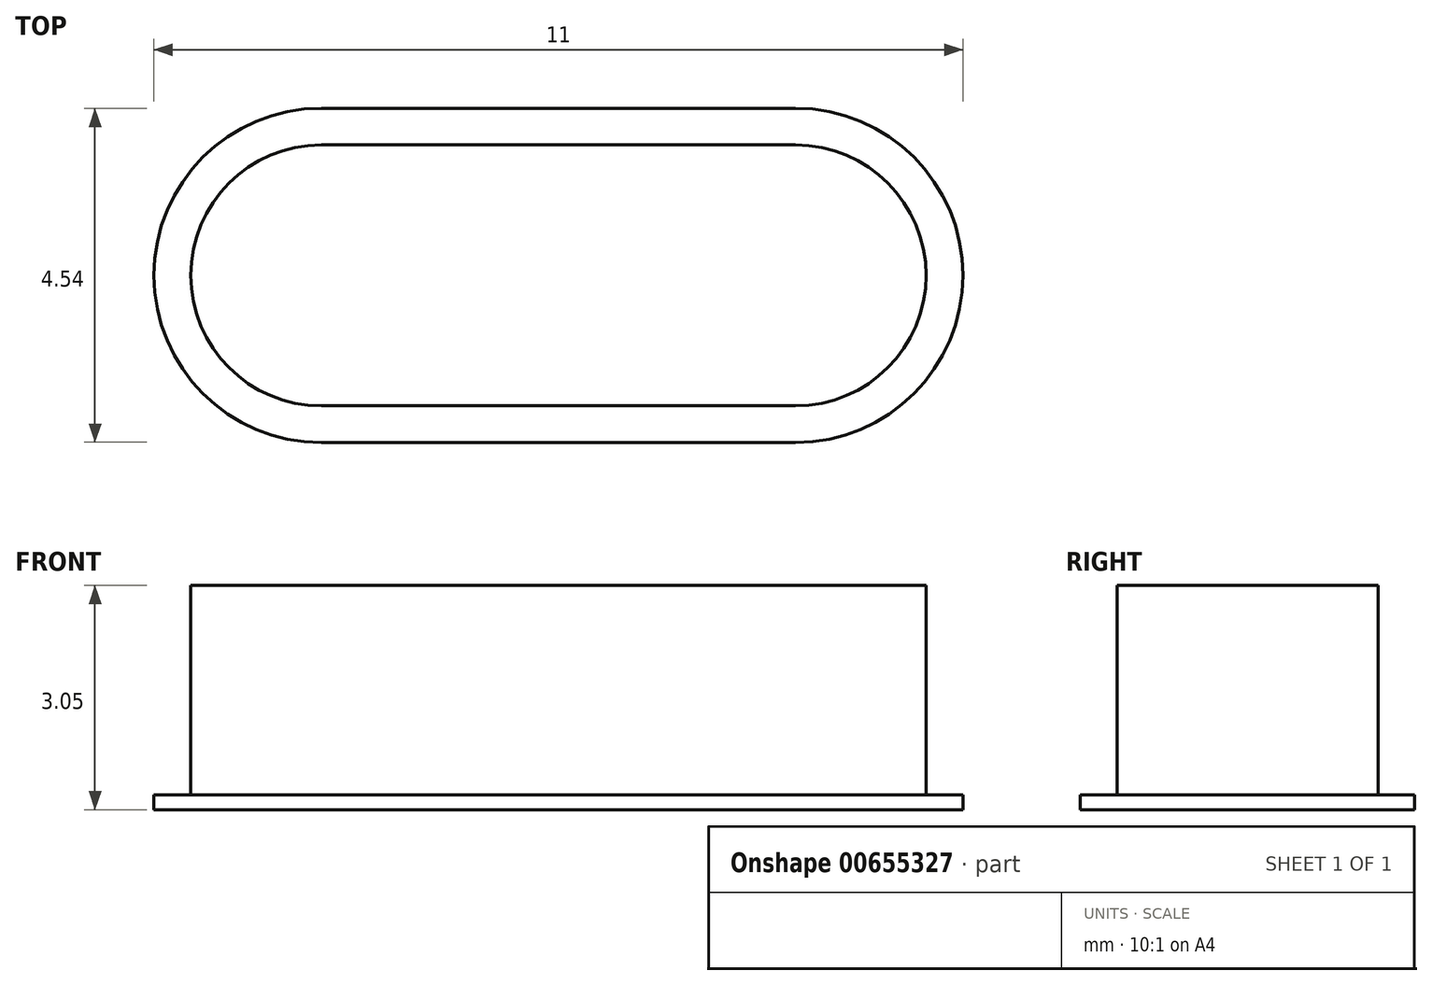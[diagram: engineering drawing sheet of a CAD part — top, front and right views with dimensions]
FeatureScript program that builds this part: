
annotation { "Feature Type Name" : "Feature", "Feature Type Description" : "" }
export const myFeature = defineFeature(function(context is Context, id is Id, definition is map)
    precondition{}
    {
        {
            var Q0;
            Q0=qCreatedBy(makeId("Top.planeOp"),FACE);
            var sketch = newSketch(context, id + "F0", { "sketchPlane" : qUnion([Q0])});
            skLineSegment(sketch, "E0.bottom", {"start": v(3.22, -1.77) * mm, "end": v(-3.22, -1.78) * mm});
            skLineSegment(sketch, "E0.top", {"start": v(3.22, 1.78) * mm, "end": v(-3.22, 1.77) * mm});
            skLineSegment(sketch, "E0.left", {"start": v(3.22, -1.77) * mm, "end": v(3.22, 1.77) * mm, "construction": true});
            skLineSegment(sketch, "E0.right", {"start": v(-3.22, -1.77) * mm, "end": v(-3.23, 1.77) * mm, "construction": true});
            skPoint(sketch, "E0.middle", {"position": v(0, 0) * mm});
            skArc(sketch, "E1", {"start": v(3.22, -1.77) * mm, "mid": v(5, 0) * mm, "end": v(3.22, 1.77) * mm});
            skArc(sketch, "E2", {"start": v(-3.23, 1.78) * mm, "mid": v(-5, 0) * mm, "end": v(-3.22, -1.78) * mm});
            skPoint(sketch, "E3", {"position": v(-5, 0) * mm});
            skPoint(sketch, "E4", {"position": v(5, 0) * mm});
            skSolve(sketch);
        }
        {
            var Q0;
            Q0=qSketchRegion(id+"F0",true);
            extrude(context, id + "F1", {"entities" : qUnion([Q0]), "depth" : 2.85 * mm, "offsetDistance" : 25 * mm});
        }
        {
            var Q0;
            Q0=makeQuery(id+"F1.opExtrude","CAP_FACE",FACE,{"disambiguationData":[OSD([sQuery(id+"F0.wireOp",EDGE,"E0.bottom"),sQuery(id+"F0.wireOp",EDGE,"E0.top"),sQuery(id+"F0.wireOp",EDGE,"E1"),sQuery(id+"F0.wireOp",EDGE,"E2")])],"isStart":true});
            var sketch = newSketch(context, id + "F2", { "sketchPlane" : qUnion([Q0])});
            skArc(sketch, "E5.0", {"start": v(3.22, -2.27) * mm, "mid": v(5.5, 0) * mm, "end": v(3.22, 2.27) * mm});
            skLineSegment(sketch, "E5.1", {"start": v(-3.23, -2.27) * mm, "end": v(3.22, -2.28) * mm});
            skArc(sketch, "E5.2", {"start": v(-3.22, 2.28) * mm, "mid": v(-5.5, 0) * mm, "end": v(-3.23, -2.28) * mm});
            skLineSegment(sketch, "E5.3", {"start": v(3.22, 2.28) * mm, "end": v(-3.22, 2.28) * mm});
            skSolve(sketch);
        }
        {
            var Q0;
            Q0=qSketchRegion(id+"F2",true);
            extrude(context, id + "F3", {"entities" : qUnion([Q0]), "operationType" : NewBodyOperationType.ADD, "depth" : .2 * mm, "offsetDistance" : 25 * mm});
        }
        {
            var Q0;
            Q0=makeQuery(id+"F1.opExtrude","SWEPT_EDGE",EDGE,{"disambiguationData":[OSD([sQuery(id+"F0.wireOp",EDGE,"E0.bottom"),sQuery(id+"F0.wireOp",EDGE,"E2")])]});
            var Q1;
            Q1=makeQuery(id+"F1.opExtrude","SWEPT_EDGE",EDGE,{"disambiguationData":[OSD([sQuery(id+"F0.wireOp",EDGE,"E0.top"),sQuery(id+"F0.wireOp",EDGE,"E2")])]});
            cPlane(context, id + "F4", {"entities" : qUnion([Q0, Q1]), "cplaneType" : CPlaneType.LINE_ANGLE, "offset" : 25 * mm, "angle" : 0 * degree, "width" : 150 * mm, "height" : 150 * mm});
        }
        {
            var Q0;
            Q0=makeQuery(id+"F1.opExtrude","CAP_FACE",FACE,{"disambiguationData":[OSD([sQuery(id+"F0.wireOp",EDGE,"E0.bottom"),sQuery(id+"F0.wireOp",EDGE,"E0.top"),sQuery(id+"F0.wireOp",EDGE,"E1"),sQuery(id+"F0.wireOp",EDGE,"E2")])],"isStart":false});
            var sketch = newSketch(context, id + "F5", { "sketchPlane" : qUnion([Q0])});
            skLineSegment(sketch, "E6", {"start": v(-3.22, 1.78) * mm, "end": v(-3.22, -1.78) * mm, "construction": true});
            skLineSegment(sketch, "E7", {"start": v(-3.22, 0) * mm, "end": v(-5, 0) * mm, "construction": true});
            skSolve(sketch);
        }
    });
